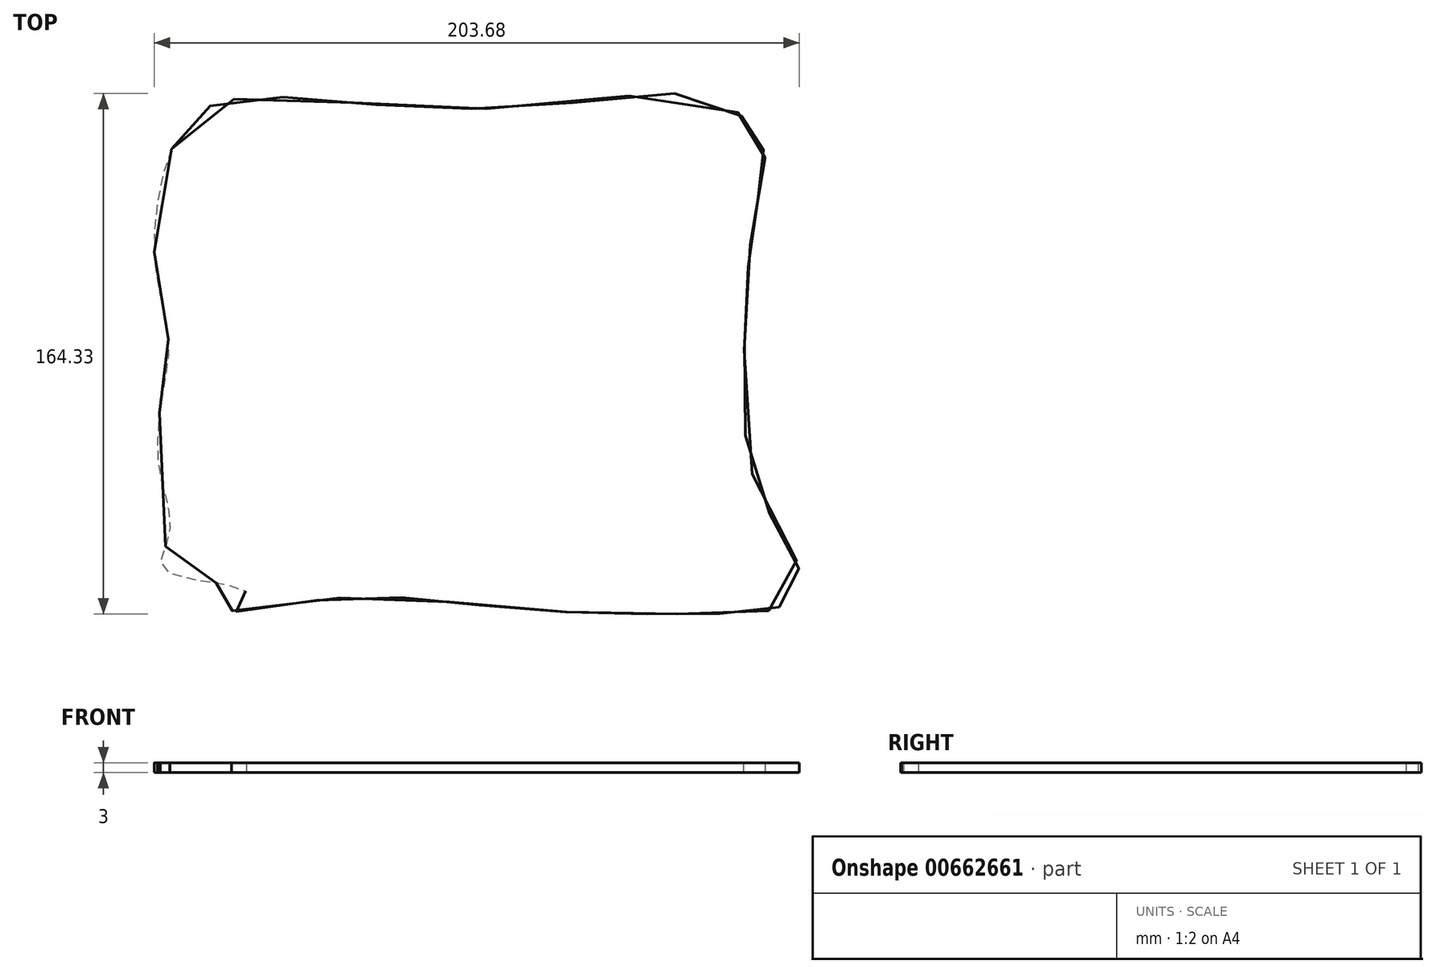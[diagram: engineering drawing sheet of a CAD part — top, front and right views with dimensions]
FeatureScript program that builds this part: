
annotation { "Feature Type Name" : "Feature", "Feature Type Description" : "" }
export const myFeature = defineFeature(function(context is Context, id is Id, definition is map)
    precondition{}
    {
        {
            var Q0;
            Q0=qCreatedBy(makeId("Top.planeOp"),FACE);
            var sketch = newSketch(context, id + "F0", { "sketchPlane" : qUnion([Q0])});
            skFitSpline(sketch, "E0", {"points": [v(-82.66, 57.43) * mm, v(-87.97, 21.58) * mm, v(-83.65, -2.99) * mm, v(-85.64, -19.92) * mm, v(-86.97, -41.16) * mm, v(-84.32, -53.44) * mm, v(-83.98, -66.4) * mm, v(-84.98, -75.68) * mm, v(-59.13, -82.66) * mm, v(-63.73, -87.97) * mm, v(-33.2, -84.65) * mm, v(7.97, -85.98) * mm, v(54.1, -89.3) * mm, v(89.96, -89.3) * mm, v(110.87, -86.3) * mm, v(115.19, -74.69) * mm, v(101.9, -49.46) * mm, v(98.26, 0) * mm, v(100.91, 34.2) * mm, v(104.56, 55.77) * mm, v(102.9, 58.7) * mm, v(92.28, 71.7) * mm, v(37.84, 71.37) * mm, v(-22.57, 71.7) * mm, v(-67.72, 72.03) * mm, v(-82.66, 57.43) * mm]});
            skSolve(sketch);
        }
        {
            var Q0;
            Q0=makeQuery(id+"F0.imprint","IMPRINT",FACE,{"disambiguationData":[TD([[makeQuery(id+"F0.imprint","IMPRINT",EDGE,{"derivedFrom":sQuery(id+"F0.wireOp",EDGE,"E0")}),1.0]])]});
            extrude(context, id + "F1", {"entities" : qUnion([Q0]), "depth" : 3 * mm, "offsetDistance" : 25 * mm});
        }
    });
